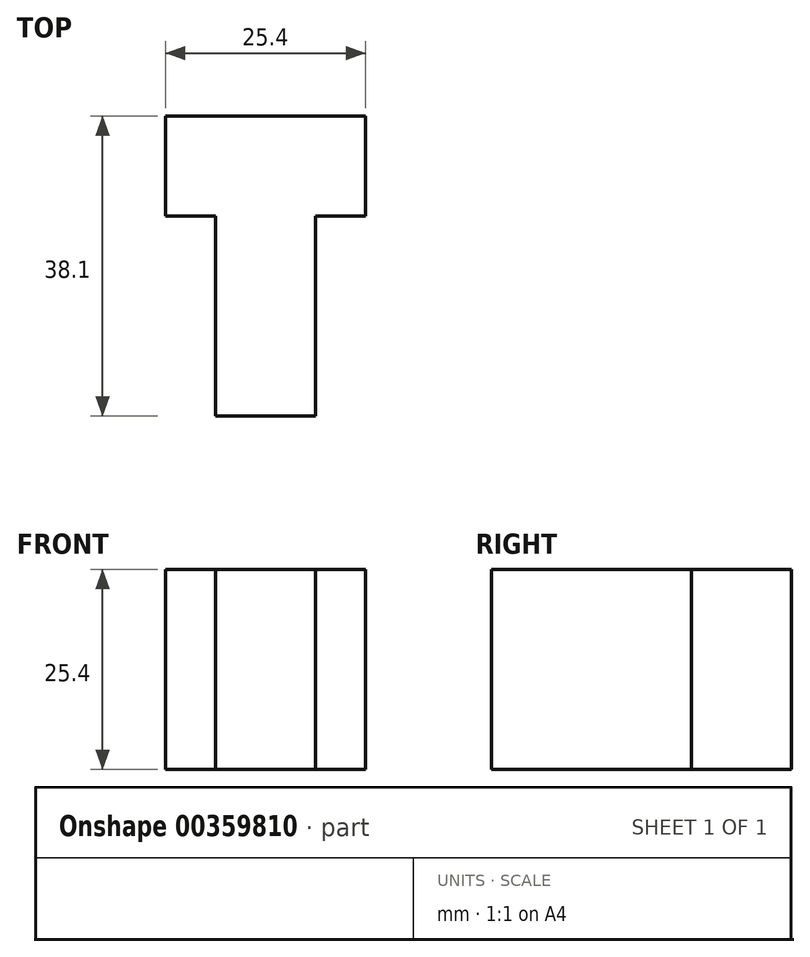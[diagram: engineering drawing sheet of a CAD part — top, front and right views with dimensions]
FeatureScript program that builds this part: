
annotation { "Feature Type Name" : "Feature", "Feature Type Description" : "" }
export const myFeature = defineFeature(function(context is Context, id is Id, definition is map)
    precondition{}
    {
        {
            var Q0;
            Q0=qCreatedBy(makeId("Top.planeOp"),FACE);
            var sketch = newSketch(context, id + "F0", { "sketchPlane" : qUnion([Q0])});
            skLineSegment(sketch, "E0", {"start": v(0, 0) * mm, "end": v(0, 12.7) * mm});
            skLineSegment(sketch, "E1", {"start": v(0, 12.7) * mm, "end": v(25.4, 12.7) * mm});
            skLineSegment(sketch, "E2", {"start": v(25.4, 12.7) * mm, "end": v(25.4, 0) * mm});
            skLineSegment(sketch, "E3", {"start": v(25.4, 0) * mm, "end": v(19.05, 0) * mm});
            skLineSegment(sketch, "E4", {"start": v(19.05, 0) * mm, "end": v(19.05, -25.4) * mm});
            skLineSegment(sketch, "E5", {"start": v(6.35, -25.4) * mm, "end": v(6.35, 0) * mm});
            skLineSegment(sketch, "E6", {"start": v(6.35, 0) * mm, "end": v(0, 0) * mm});
            skLineSegment(sketch, "E7", {"start": v(6.35, -25.4) * mm, "end": v(19.05, -25.4) * mm});
            skSolve(sketch);
        }
        {
            var Q0;
            Q0 = qSketchRegion(id + "F0", true);
            extrude(context, id + "F1", {"entities" : qUnion([Q0]), "depth" : 25.4 * mm});
        }
    });
